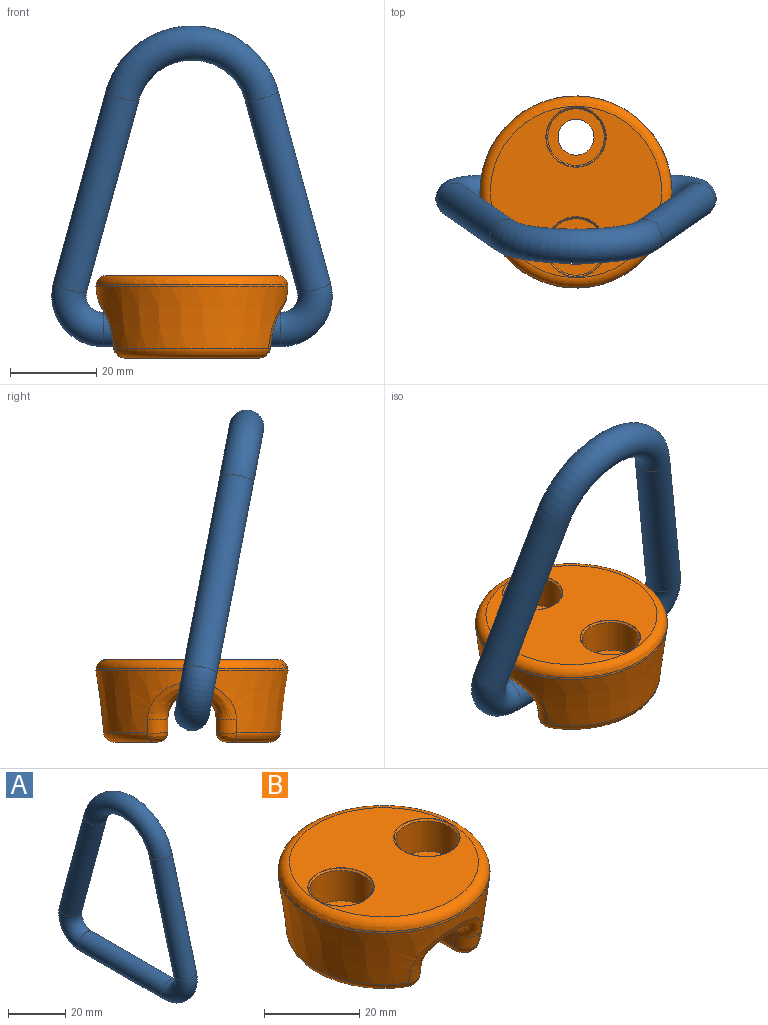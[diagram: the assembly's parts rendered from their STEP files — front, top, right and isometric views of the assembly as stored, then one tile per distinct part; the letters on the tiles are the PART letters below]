
ASSEMBLY  parts=2 mates=1
PART A: 6 faces, bbox 7.9x66.8x78.1 mm
  f0: cylinder r=3.97mm len=47.18mm, axis (0,0.26,0.97), area 1164.9mm2, adj f1,f5
  f1: torus R=7.94mm, axis (-1,0,0), area 362.7mm2, adj f0,f2
  f2: cylinder r=3.97mm len=41.05mm, axis (0,-1,0), area 1023.6mm2, adj f1,f3
  f3: torus R=7.94mm, axis (-1,0,0), area 362.7mm2, adj f2,f4
  f4: cylinder r=3.97mm len=47.18mm, axis (0,0.26,-0.97), area 1164.9mm2, adj f3,f5
  f5: torus R=16.67mm, axis (1,0,0), area 1088.2mm2, adj f0,f4
PART B: 44 faces, bbox 48x48x32 mm
  f0: plane 39.61x39.61mm, normal (0,0,1), area 926.8mm2, adj f22,f42,f43
  f1: cylinder r=5.56mm len=30.74mm, axis (0,1,0), area 274.6mm2, adj f6,f7,f9,f12,f32,f33,f34,f35
  f2: plane 31.44x10.14mm, normal (0,0,-1), area 170mm2, adj f14,f15,f16,f17,f39
  f3: cone r=22.23mm half-angle=7deg, axis (0,0,-1), area 63.1mm2, adj f4,f22
  f4: cone r=22.23mm half-angle=7deg, axis (0,0,1), area 1520.3mm2, adj f3,f8,f9,f10,f11,f12,f13,f16
  f5: plane 31.44x10.14mm, normal (0,0,-1), area 170mm2, adj f18,f19,f20,f21,f38
  f6: plane 30.74x3.18mm, normal (1,0,0), area 96.2mm2, adj f1,f8,f13,f15
  f7: plane 30.74x3.18mm, normal (-1,0,0), area 96.2mm2, adj f1,f10,f11,f20
  f8: bspline ~26.1x8.53mm, area 21mm2, adj f4,f6,f9,f17
  f9: bspline ~20.6x10.49mm, area 128mm2, adj f1,f4,f8,f10
  f10: bspline ~32.03x9.37mm, area 20.9mm2, adj f4,f7,f9,f21
  f11: bspline ~26.1x8.53mm, area 21mm2, adj f4,f7,f12,f18
  f12: bspline ~20.6x10.49mm, area 128mm2, adj f1,f4,f11,f13
  f13: bspline ~32.03x9.37mm, area 20.9mm2, adj f4,f6,f12,f14
  f14: bspline ~5.36x3.34mm, area 16.6mm2, adj f2,f13,f15,f16
  f15: cylinder r=2.39mm len=29.84mm, axis (0,-1,0), area 111.9mm2, adj f2,f6,f14,f17
  f16: torus R=18.09mm, axis (0,0,-1), area 140.7mm2, adj f2,f4,f14,f17
  f17: bspline ~5.37x3.89mm, area 16.6mm2, adj f2,f8,f15,f16
  f18: bspline ~5.37x3.89mm, area 16.6mm2, adj f5,f11,f19,f20
  f19: torus R=18.09mm, axis (0,0,-1), area 140.7mm2, adj f4,f5,f18,f21
  f20: cylinder r=2.39mm len=29.84mm, axis (0,1,0), area 111.9mm2, adj f5,f7,f18,f21
  f21: bspline ~5.36x3.34mm, area 16.6mm2, adj f5,f10,f19,f20
  f22: torus R=19.81mm, axis (0,0,1), area 460.6mm2, adj f0,f3
  f23: cylinder r=6.54mm len=13.08mm, axis (0,0,1), area 320.5mm2, adj f24,f41
  f24: plane 13.08x13.08mm, normal (0,0,1), area 79.9mm2, adj f23,f25
  f25: cylinder r=4.17mm len=10.49mm, axis (0,0,1), area 274.6mm2, adj f24,f38
  f26: cylinder r=6.54mm len=13.08mm, axis (0,0,1), area 320.5mm2, adj f27,f40
  f27: plane 13.08x13.08mm, normal (0,0,1), area 79.9mm2, adj f26,f28
  f28: cylinder r=4.17mm len=10.49mm, axis (0,0,1), area 274.6mm2, adj f27,f39
  f29: cylinder r=5.56mm len=14.86mm, axis (0,-1,0), area 273.5mm2, adj f30,f31,f32,f37
  f30: torus R=5.05mm, axis (0,-1,0), area 7.2mm2, adj f29,f34,f36
  f31: torus R=5.05mm, axis (0,-1,0), area 7.2mm2, adj f29,f33,f35
  f32: cylinder r=0.51mm len=14.86mm, axis (0,1,0), area 1.3mm2, adj f1,f29,f33,f34
  f33: bspline ~5.89x5.61mm, area 5mm2, adj f1,f31,f32,f35
  f34: bspline ~6.89x5.61mm, area 5mm2, adj f1,f30,f32,f36
  f35: bspline ~6.89x5.61mm, area 5mm2, adj f1,f31,f33,f37
  f36: bspline ~6.89x5.61mm, area 5mm2, adj f1,f30,f34,f37
  f37: cylinder r=0.51mm len=14.86mm, axis (0,-1,0), area 1.3mm2, adj f1,f29,f35,f36
  f38: cone r=4.55mm half-angle=45deg, axis (0,0,-1), area 14.7mm2, adj f5,f25
  f39: cone r=4.55mm half-angle=45deg, axis (0,0,-1), area 14.7mm2, adj f2,f28
  f40: cone r=6.54mm half-angle=45deg, axis (0,0,1), area 20.5mm2, adj f26,f43
  f41: cone r=6.54mm half-angle=45deg, axis (0,0,1), area 20.5mm2, adj f23,f42
  f42: torus R=6.97mm, axis (0,0,1), area 4.3mm2, adj f0,f41
  f43: torus R=6.97mm, axis (0,0,1), area 4.3mm2, adj f0,f40
PLACE A rot(axis=(0.09,0.09,-0.99),90.5deg) t=(0,-12.65,72.85)mm
PLACE B rot(axis=(0,0,1),90deg) t=(0,0,16.51)mm fixed
MATE revolute A.f2 <-> B.f29  axis (-1,0,0) through (0,0,6.58)mm
